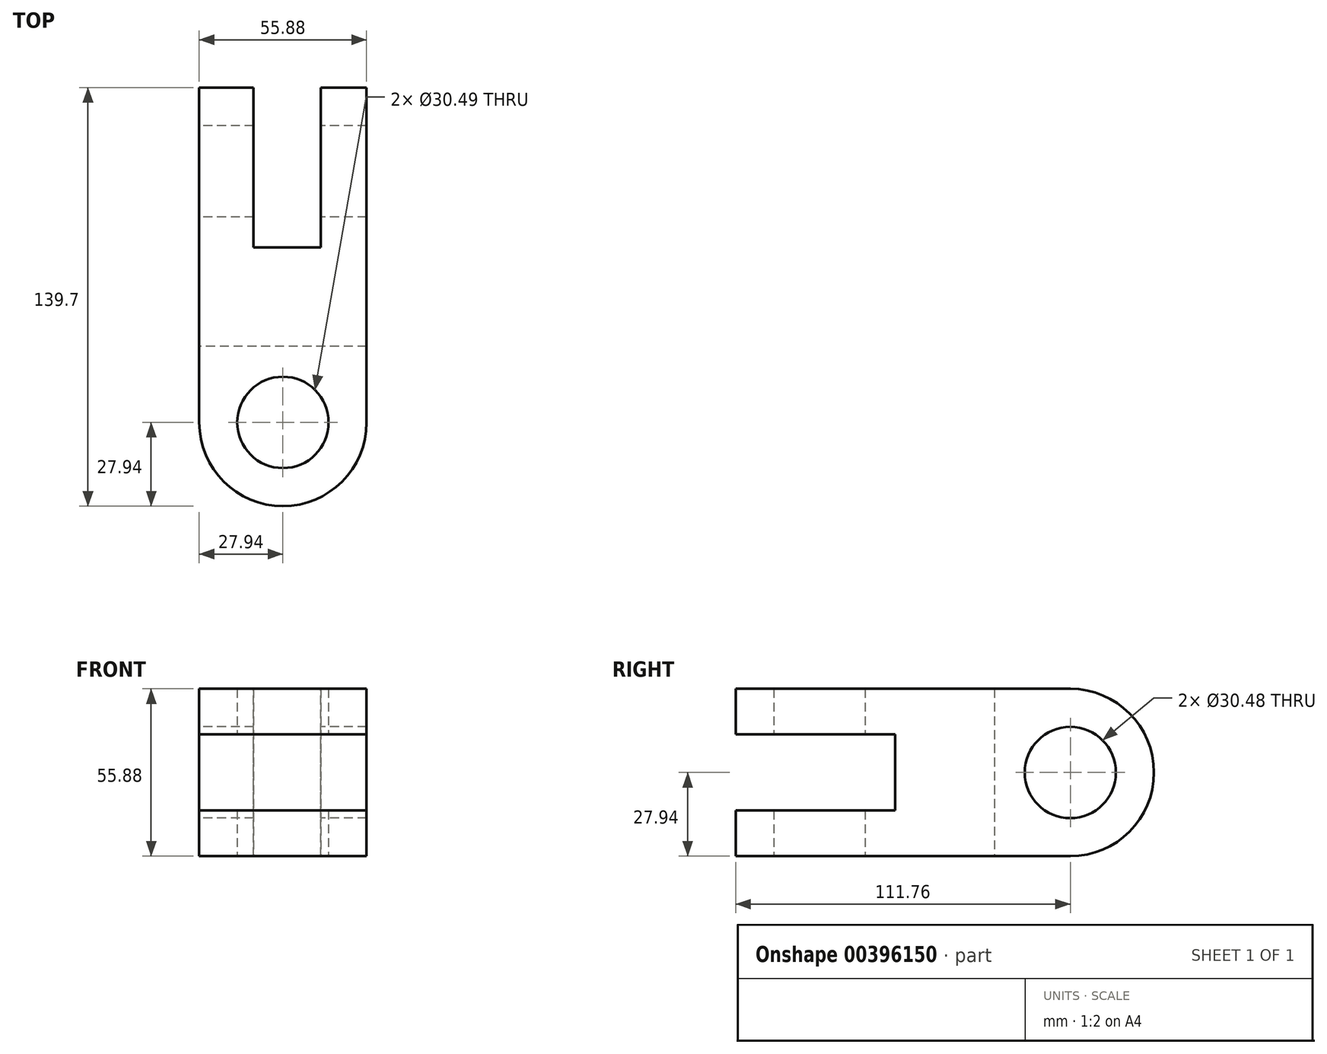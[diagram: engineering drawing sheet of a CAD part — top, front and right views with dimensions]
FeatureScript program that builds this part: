
annotation { "Feature Type Name" : "Feature", "Feature Type Description" : "" }
export const myFeature = defineFeature(function(context is Context, id is Id, definition is map)
    precondition{}
    {
        {
            var Q0;
            Q0=qCreatedBy(makeId("Front.planeOp"),FACE);
            var sketch = newSketch(context, id + "F0", { "sketchPlane" : qUnion([Q0])});
            skLineSegment(sketch, "E0.bottom", {"start": v(0, 0) * mm, "end": v(55.88, 0) * mm});
            skLineSegment(sketch, "E0.top", {"start": v(0, -55.88) * mm, "end": v(55.88, -55.88) * mm});
            skLineSegment(sketch, "E0.left", {"start": v(0, 0) * mm, "end": v(0, -55.88) * mm});
            skLineSegment(sketch, "E0.right", {"start": v(55.88, 0) * mm, "end": v(55.88, -55.88) * mm});
            skSolve(sketch);
        }
        {
            var Q0;
            Q0 = qSketchRegion(id + "F0", true);
            extrude(context, id + "F1", {"entities" : qUnion([Q0]), "depth" : 139.7 * mm});
        }
        {
            var Q0;
            Q0=makeQuery(id+"F1.opExtrude","CAP_EDGE",EDGE,{"disambiguationData":[OSD([sQuery(id+"F0.wireOp",EDGE,"E0.left")])],"isStart":false});
            var Q1;
            Q1=makeQuery(id+"F1.opExtrude","CAP_EDGE",EDGE,{"disambiguationData":[OSD([sQuery(id+"F0.wireOp",EDGE,"E0.bottom")])],"isStart":true});
            var Q2;
            Q2=makeQuery(id+"F1.opExtrude","CAP_EDGE",EDGE,{"disambiguationData":[OSD([sQuery(id+"F0.wireOp",EDGE,"E0.top")])],"isStart":true});
            var Q3;
            Q3=makeQuery(id+"F1.opExtrude","CAP_EDGE",EDGE,{"disambiguationData":[OSD([sQuery(id+"F0.wireOp",EDGE,"E0.right")])],"isStart":false});
            fillet(context, id + "F2", {"entities" : qUnion([Q0, Q1, Q2, Q3]), "radius" : 27.94 * mm, "tangentPropagation" : true, "allowEdgeOverflow" : false});
        }
        {
            var Q0;
            Q0=makeQuery(id+"F1.opExtrude","SWEPT_FACE",FACE,{"disambiguationData":[OSD([sQuery(id+"F0.wireOp",EDGE,"E0.top")])]});
            var sketch = newSketch(context, id + "F3", { "sketchPlane" : qUnion([Q0])});
            skLineSegment(sketch, "E1.bottom", {"start": v(18.15, -7.63) * mm, "end": v(40.64, -7.63) * mm});
            skLineSegment(sketch, "E1.top", {"start": v(18.15, 53.34) * mm, "end": v(40.64, 53.34) * mm});
            skLineSegment(sketch, "E1.left", {"start": v(18.15, -7.63) * mm, "end": v(18.15, 53.34) * mm});
            skLineSegment(sketch, "E1.right", {"start": v(40.64, -7.63) * mm, "end": v(40.64, 53.34) * mm});
            skSolve(sketch);
        }
        {
            var Q0;
            {var subQ0=sQuery(id+"F3.wireOp",EDGE,"E1.bottom");Q0=makeQuery(id+"F3.imprint","IMPRINT",FACE,{"disambiguationData":[TD([[makeQuery(id+"F3.imprint","IMPRINT",EDGE,{"derivedFrom":subQ0}),1.0]])]});}
            var Q1;
            {var subQ0=sQuery(id+"F3.wireOp",EDGE,"E1.top");Q1=makeQuery(id+"F3.imprint","IMPRINT",FACE,{"disambiguationData":[TD([[makeQuery(id+"F3.imprint","IMPRINT",EDGE,{"derivedFrom":subQ0}),-1.0]])]});}
            var Q2;
            Q2 = qSketchRegion(id + "Fq74EP2sgeeN2JT_1", true);
            extrude(context, id + "F4", {"entities" : qUnion([Q0, Q1, Q2]), "operationType" : NewBodyOperationType.REMOVE, "endBound" : BoundingType.THROUGH_ALL, "oppositeDirection" : true, "depth" : 25.4 * mm});
        }
        {
            var Q0;
            Q0=makeQuery(id+"F1.opExtrude","SWEPT_FACE",FACE,{"disambiguationData":[OSD([sQuery(id+"F0.wireOp",EDGE,"E0.left")])]});
            var sketch = newSketch(context, id + "F5", { "sketchPlane" : qUnion([Q0])});
            skCircle(sketch, "E2", {"center": v(27.94, -27.94) * mm, "radius": 15.24 * mm});
            skSolve(sketch);
        }
        {
            var Q0;
            Q0 = qSketchRegion(id + "F5", true);
            extrude(context, id + "F6", {"entities" : qUnion([Q0]), "operationType" : NewBodyOperationType.REMOVE, "endBound" : BoundingType.THROUGH_ALL, "oppositeDirection" : true, "depth" : 25.4 * mm});
        }
        {
            var Q0;
            Q0=makeQuery(id+"F1.opExtrude","SWEPT_FACE",FACE,{"disambiguationData":[OSD([sQuery(id+"F0.wireOp",EDGE,"E0.left")])]});
            var sketch = newSketch(context, id + "F7", { "sketchPlane" : qUnion([Q0])});
            skLineSegment(sketch, "E3.bottom", {"start": v(170.69, -40.64) * mm, "end": v(86.36, -40.64) * mm});
            skLineSegment(sketch, "E3.top", {"start": v(170.69, -15.24) * mm, "end": v(86.36, -15.24) * mm});
            skLineSegment(sketch, "E3.left", {"start": v(170.69, -40.64) * mm, "end": v(170.69, -15.24) * mm});
            skLineSegment(sketch, "E3.right", {"start": v(86.36, -40.64) * mm, "end": v(86.36, -15.24) * mm});
            skSolve(sketch);
        }
        {
            var Q0;
            Q0 = qSketchRegion(id + "F7", true);
            extrude(context, id + "F8", {"entities" : qUnion([Q0]), "operationType" : NewBodyOperationType.REMOVE, "endBound" : BoundingType.THROUGH_ALL, "oppositeDirection" : true, "depth" : 25.4 * mm});
        }
        {
            var Q0;
            Q0=makeQuery(id+"F1.opExtrude","SWEPT_FACE",FACE,{"disambiguationData":[OSD([sQuery(id+"F0.wireOp",EDGE,"E0.top")])]});
            var sketch = newSketch(context, id + "F9", { "sketchPlane" : qUnion([Q0])});
            skCircle(sketch, "E4", {"center": v(27.94, 111.76) * mm, "radius": 15.24 * mm});
            skSolve(sketch);
        }
        {
            var Q0;
            Q0=makeQuery(id+"F9.imprint","IMPRINT",FACE,{"disambiguationData":[TD([[makeQuery(id+"F9.imprint","IMPRINT",EDGE,{"derivedFrom":sQuery(id+"F9.wireOp",EDGE,"E4")}),1.0]])]});
            extrude(context, id + "F10", {"entities" : qUnion([Q0]), "operationType" : NewBodyOperationType.REMOVE, "endBound" : BoundingType.THROUGH_ALL, "oppositeDirection" : true, "depth" : 25.4 * mm});
        }
    });
